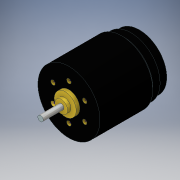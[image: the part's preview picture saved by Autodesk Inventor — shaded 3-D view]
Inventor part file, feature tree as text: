
AUTODESK INVENTOR PART (.ipt)
format: ipt  version: 2016 (Build 200138000, 138)  size: 252,928 bytes
history: native  units: mm
features: other x9, sketch x2, imported_body x1, extrude x1
ambient origin geometry x8: Origin, YZ Plane, XZ Plane, XY Plane, X Axis, Y Axis, Z Axis, Center Point
bodies: Body1 (feature_tree)
feature tree (13):
  other  "ソリッド1"
  other  "修復済みジオメトリ1"
  imported_body  "Base1"
  other  "ダイレクト編集1"
  other  "ダイレクト編集2"
  extrude  "押し出し1"  Depth=7.5mm
  sketch  "3D スケッチ1"
  sketch  "スケッチ2"
  other  "削除1"
  other  "削除2"
  other  "削除3"
  other  "削除4"
  other  "削除5"
